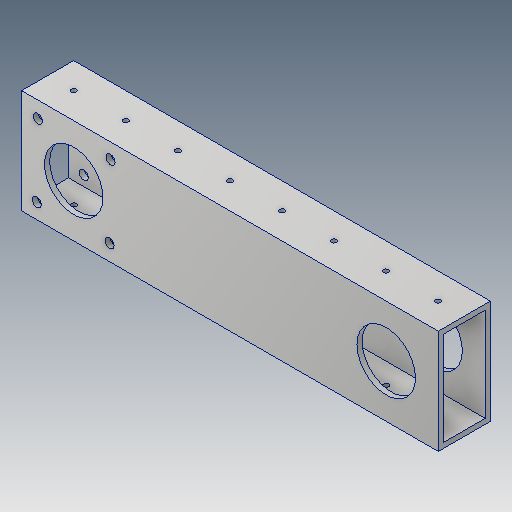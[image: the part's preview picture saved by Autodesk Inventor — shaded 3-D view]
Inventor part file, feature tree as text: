
AUTODESK INVENTOR PART (.ipt)
format: ipt  version: 2018 (Build 220112000, 112)  size: 172,544 bytes
history: native  units: in
note: dims shown in document units (in); Inventor stores cm internally (conversion verified against a paired STEP export)
features: reference x6, sketch x5, hole x4, other x4, extrude x1, shell x1
ambient origin geometry x8: Origin, YZ Plane, XZ Plane, XY Plane, X Axis, Y Axis, Z Axis, Center Point
bodies: Solid1 (feature_tree)
feature tree (21):
  extrude  "Extrusion1"  Depth=2.0in
  shell  "Shell1"  Thickness=8.0in
  hole  "Hole1"  [1 undecoded]
  hole  "Hole6"  [1 undecoded]
  hole  "Hole7"  [1 undecoded]
  hole  "Hole8"  [1 undecoded]
  sketch  "Sketch1"  dims[d0=1.0in d1=2.0in d2=8.0in d3=0.0in]
  sketch  "Sketch2"  dims[d4=0.1in d5=0.5in]
  sketch  "Sketch14"  dims[d6=0.5in d7=14.5669in d9=1.0in d10=0.3937in d12=1.0in]
  reference  "Reference3"
  sketch  "Sketch15"  dims[d14=0.1in d15=0.75in d16=0.375in d17=0.25in d18=0.5635in d19=2.0in d20=0.8108in]
  reference  "Reference4"
  sketch  "Sketch16"  dims[d90=1.125in d91=0.75in d92=0.375in d93=0.25in d94=0.5635in d95=1.0in d96=0.8108in d97=1.125in d98=0.75in d99=0.375in d100=0.25in d101=0.5635in d102=1.0in d103=0.8108in d104=0.177in d105=0.75in d106=0.332in d107=0.25in d108=0.5635in d109=1.0in d110=0.8108in]
  reference  "Reference5"
  reference  "Reference6"
  reference  "Reference7"
  reference  "Reference8"
  parser-record x1  (decoder bookkeeping rows leaked as tree rows — omitted from the tree; the rows remain in map.json)
  other  "Robot.iam"
  other  "Support Pivs 25 uppereeeeee:1"
  other  "VersaPlanetary_v2_Two_Stage_100_1_with_BAG:4"
note: 4 required parameter values undecoded (feature->parameter linkage not recoverable at this tier; creation-order binding heuristic only, values carry confidence <= 0.55)
note: 1 file-system path scrubbed to <path> (originals preserved in map.json)
